# Revit family: IS_Tesi_Multiproduct_BIM_GB;T3529;T3530
name_source: partatom
category: Plumbing Fixtures
revit_build: Autodesk Revit MEP 2012 (Build: 20110309_2315(x64)
units: mm (PartAtom-declared; Revit-internal decimal feet)

## types (2) — shared parameters
Accessories = www.idealspec.co.uk
AreaUnits = millimeters
Assembly Code = C1030200
AssetType = Fixed
BREEAMApproved = No
Brand = Ideal Standard
ConnectionType = Plumbing
Description = Tesi toilet seat and cover, slow close wrap style
DurationUnit = year
ECA = No
ExpectedLife = 5
Features = Toilet Seat And Cover, Slow Close Wrap Style
Finish = White
Help = www.idealspec.co.uk/contact-us.html
IfcExportAs = IfcSanitaryTerminalType
IfcExportType = SEAT&COVER
InstallationInstructions = www.idealspec.co.uk/resources.html
LinearUnits = millimeters
ManufacturerURL = www.idealspec.co.uk
NBSDescription = WC pans
NBSReference = 45-30-70/384
NettWeight = 2.2 Kg
NominalDepth = 446 mm
NominalHeight = 38 mm
NominalLength = 446 mm
NominalWidth = 366 mm
PanColor = White
PanMaterial = Vitreous china
PanMounting = BackToWall
Shape = Sculptured
Size = 366 x446 x38 mm
Space = Internal
ToiletPanType = WashDown
ToiletType = Other
URL = www.idealspec.co.uk
Uniclass2015Description = WC seats and covers
Uniclass2015Reference = Pr_40_20_93_95
Uniclass2015Version = Products v1.1
Version = 1
VolumeUnits = Litres
WRAS = No
WarrantyDescription = Manufacturers Warranty
WarrantyDurationParts = 5
WarrantyDurationUnit = year
WaterEfficientProduct = No
zero-valued in all types: CWFU, Cost, Default Elevation, HWFU, SpilloverLevel, WFU

## per-type parameters (varying)
| type | BIMObjectName | BarCode | Model | ModelNumber | Name | ProductInformation |
| T352901-Tesi S&C Soft Close - thin OVERWRAP | ISI_IdealStandard_WCSeats_Tesi_T3529 | 8014140430339 | T352901 | T352901 | WCSeats_Tesi_T3529_IdealStandard | www.idealspec.co.uk/assets/datasheet/T352901 |
| T353001-Tesi S&C Normal Close - thin OVERWRAP | ISI_IdealStandard_WCSeats_Tesi_T3530 | 8014140430346 | T353001 | T353001 | WCSeats_Tesi_T3530_IdealStandard | www.idealspec.co.uk/assets/datasheet/T353001 |

## geometry (parser evidence)
native form markers: Sweep x1
no freeform markers — native parametric forms only
